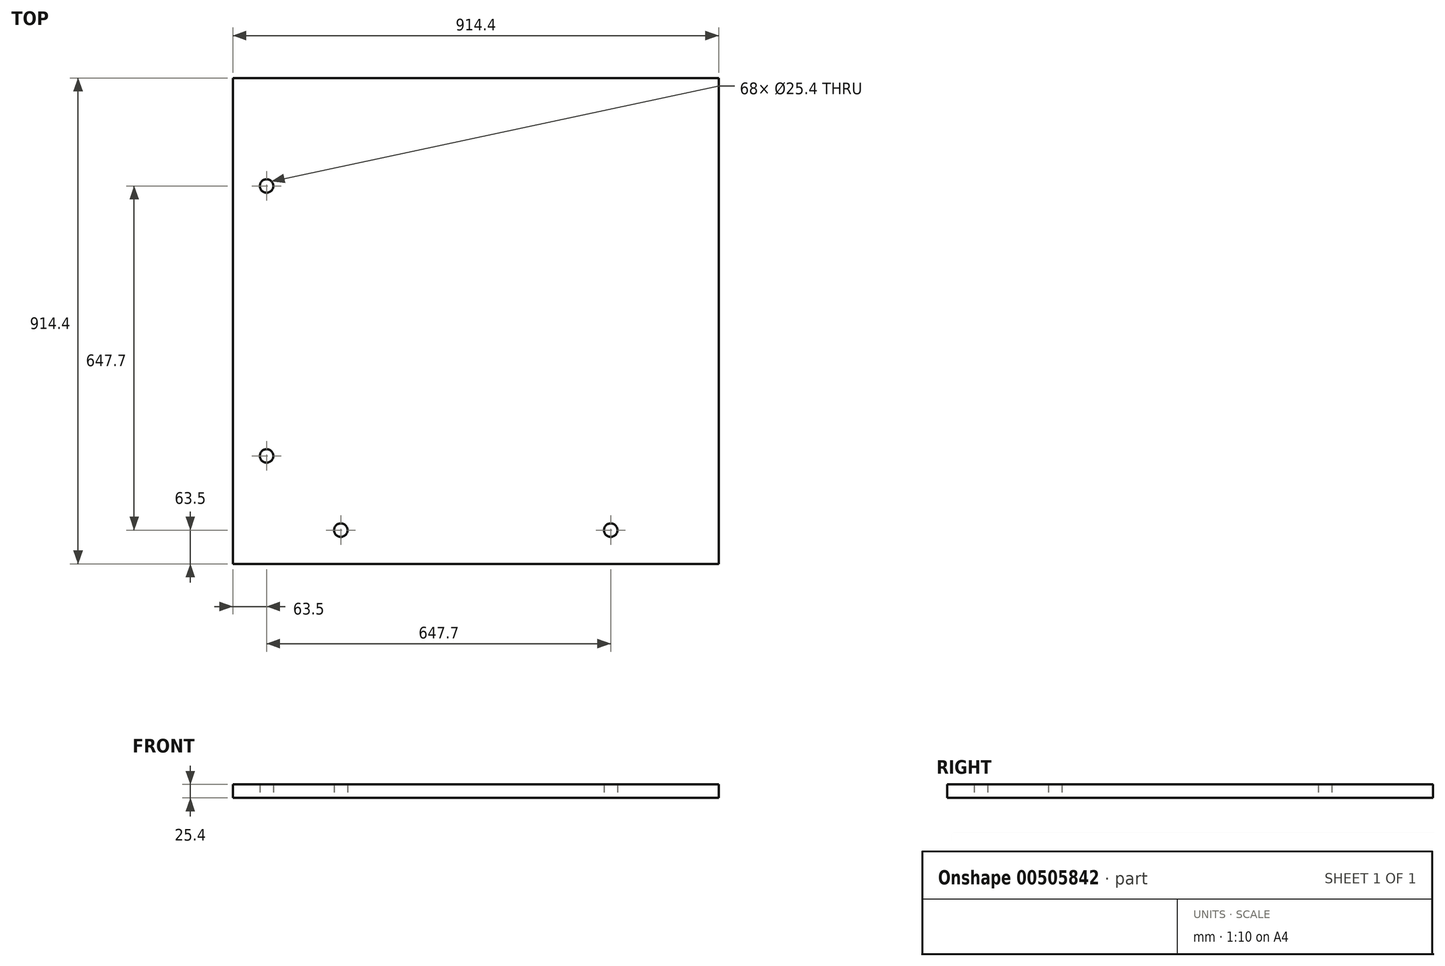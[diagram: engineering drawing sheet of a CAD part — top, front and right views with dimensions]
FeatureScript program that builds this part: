
annotation { "Feature Type Name" : "Feature", "Feature Type Description" : "" }
export const myFeature = defineFeature(function(context is Context, id is Id, definition is map)
    precondition{}
    {
        {
            var Q0;
            Q0=qCreatedBy(makeId("Top.planeOp"),FACE);
            var sketch = newSketch(context, id + "F0", { "sketchPlane" : qUnion([Q0])});
            skLineSegment(sketch, "E0.bottom", {"start": v(0, 0) * mm, "end": v(914.4, 0) * mm});
            skLineSegment(sketch, "E0.top", {"start": v(0, 914.4) * mm, "end": v(914.4, 914.4) * mm});
            skLineSegment(sketch, "E0.left", {"start": v(0, 0) * mm, "end": v(0, 914.4) * mm});
            skLineSegment(sketch, "E0.right", {"start": v(914.4, 0) * mm, "end": v(914.4, 914.4) * mm});
            skLineSegment(sketch, "E1", {"start": v(0, 0) * mm, "end": v(0, 203.2) * mm, "construction": true});
            skLineSegment(sketch, "E2", {"start": v(0, 203.2) * mm, "end": v(914.4, 203.2) * mm, "construction": true});
            skLineSegment(sketch, "E3", {"start": v(0, 0) * mm, "end": v(203.2, 0) * mm, "construction": true});
            skLineSegment(sketch, "E4", {"start": v(203.2, 0) * mm, "end": v(203.2, 914.4) * mm, "construction": true});
            skLineSegment(sketch, "E5", {"start": v(0, 0) * mm, "end": v(63.5, 0) * mm, "construction": true});
            skLineSegment(sketch, "E6", {"start": v(0, 0) * mm, "end": v(0, 63.5) * mm, "construction": true});
            skLineSegment(sketch, "E7", {"start": v(63.5, 0) * mm, "end": v(63.5, 914.4) * mm, "construction": true});
            skLineSegment(sketch, "E8", {"start": v(0, 63.5) * mm, "end": v(934.2, 63.5) * mm, "construction": true});
            skLineSegment(sketch, "E9", {"start": v(914.4, 914.4) * mm, "end": v(711.2, 914.4) * mm, "construction": true});
            skLineSegment(sketch, "E10", {"start": v(711.2, 914.4) * mm, "end": v(711.2, 0) * mm, "construction": true});
            skLineSegment(sketch, "E11", {"start": v(0, 914.4) * mm, "end": v(0, 711.2) * mm, "construction": true});
            skLineSegment(sketch, "E12", {"start": v(0, 711.2) * mm, "end": v(914.4, 711.2) * mm, "construction": true});
            skCircle(sketch, "E13", {"center": v(63.5, 711.2) * mm, "radius": 12.7 * mm});
            skCircle(sketch, "E14", {"center": v(63.5, 203.2) * mm, "radius": 12.7 * mm});
            skCircle(sketch, "E15", {"center": v(203.2, 63.5) * mm, "radius": 12.7 * mm});
            skCircle(sketch, "E16", {"center": v(711.2, 63.5) * mm, "radius": 12.7 * mm});
            skSolve(sketch);
        }
        {
            var Q0;
            Q0=makeQuery(id+"F0.imprint","IMPRINT",FACE,{"disambiguationData":[TD([[makeQuery(id+"F0.imprint","IMPRINT",EDGE,{"derivedFrom":sQuery(id+"F0.wireOp",EDGE,"E0.bottom")}),1.0]])]});
            extrude(context, id + "F1", {"entities" : qUnion([Q0]), "depth" : 25.4 * mm});
        }
    });
